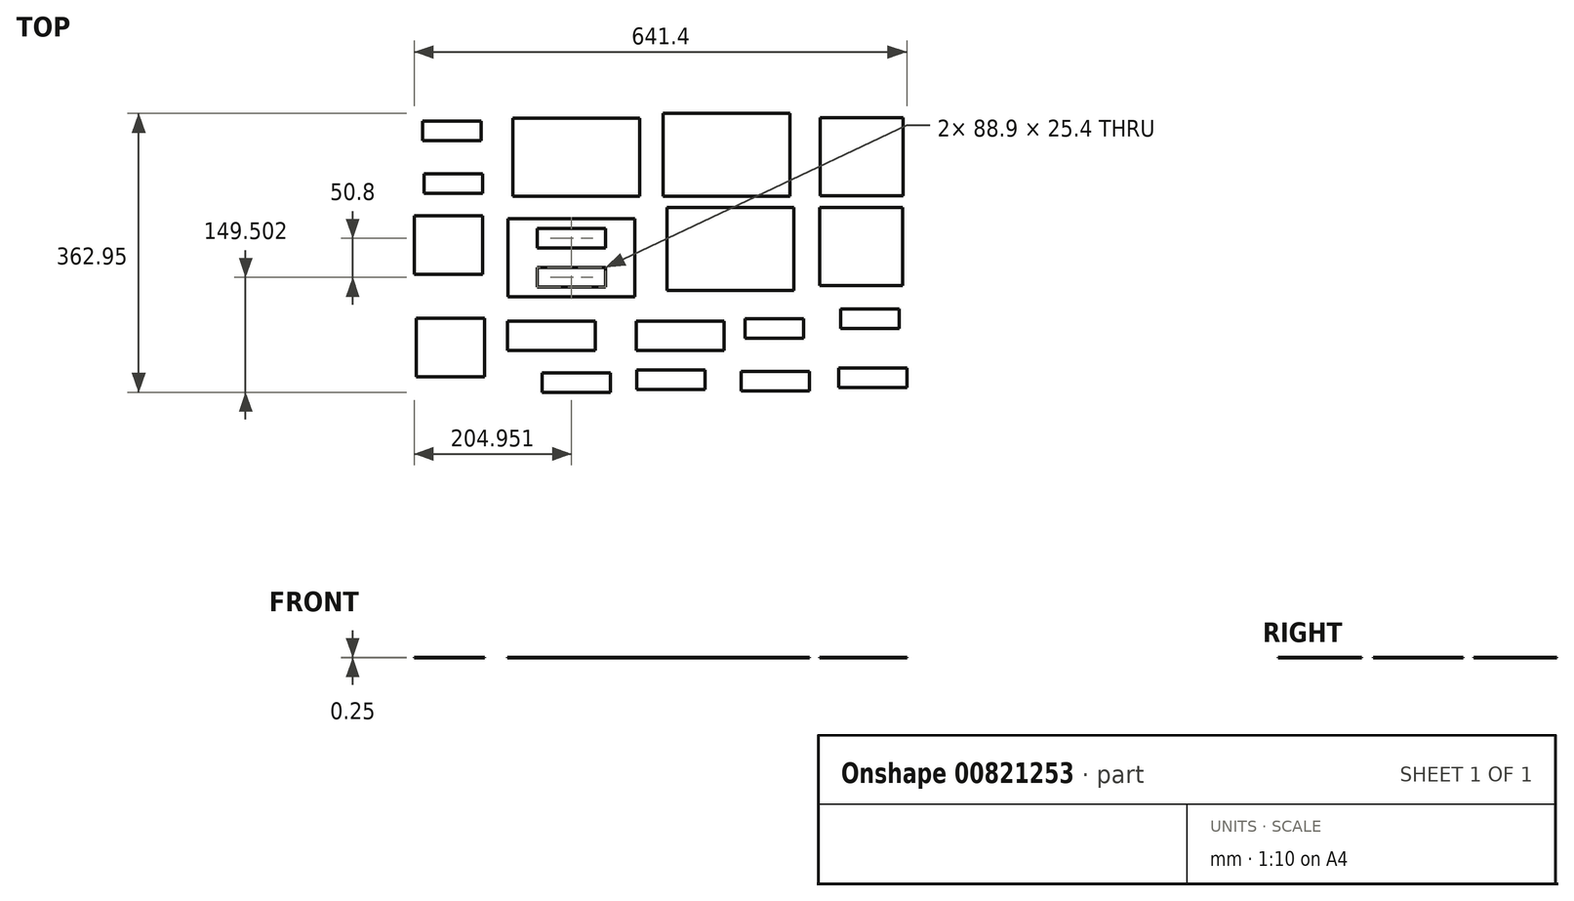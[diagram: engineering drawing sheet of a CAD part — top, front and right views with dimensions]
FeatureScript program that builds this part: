
annotation { "Feature Type Name" : "Feature", "Feature Type Description" : "" }
export const myFeature = defineFeature(function(context is Context, id is Id, definition is map)
    precondition{}
    {
        {
            assignVariable(context, id + "F0", {"name" : "th", "anyValue" : .25});
        }
        {
            var Q0;
            Q0=qCreatedBy(makeId("Top.planeOp"),FACE);
            var sketch = newSketch(context, id + "F1", { "sketchPlane" : qUnion([Q0])});
            skLineSegment(sketch, "E0.bottom", {"start": v(-461.23, 112.07) * mm, "end": v(-385.03, 112.07) * mm});
            skLineSegment(sketch, "E0.top", {"start": v(-461.23, 86.67) * mm, "end": v(-385.03, 86.67) * mm});
            skLineSegment(sketch, "E0.left", {"start": v(-461.23, 112.07) * mm, "end": v(-461.23, 86.67) * mm});
            skLineSegment(sketch, "E0.right", {"start": v(-385.03, 112.07) * mm, "end": v(-385.03, 86.67) * mm});
            skLineSegment(sketch, "E1.bottom", {"start": v(-459.53, 44.07) * mm, "end": v(-383.33, 44.07) * mm});
            skLineSegment(sketch, "E1.top", {"start": v(-459.53, 18.67) * mm, "end": v(-383.33, 18.67) * mm});
            skLineSegment(sketch, "E1.left", {"start": v(-459.53, 44.07) * mm, "end": v(-459.53, 18.67) * mm});
            skLineSegment(sketch, "E1.right", {"start": v(-383.33, 44.07) * mm, "end": v(-383.33, 18.67) * mm});
            skLineSegment(sketch, "E2.bottom", {"start": v(-472.28, -10.53) * mm, "end": v(-383.38, -10.53) * mm});
            skLineSegment(sketch, "E2.top", {"start": v(-472.28, -86.73) * mm, "end": v(-383.38, -86.73) * mm});
            skLineSegment(sketch, "E2.left", {"start": v(-472.28, -10.53) * mm, "end": v(-472.28, -86.73) * mm});
            skLineSegment(sketch, "E2.right", {"start": v(-383.38, -10.53) * mm, "end": v(-383.38, -86.73) * mm});
            skLineSegment(sketch, "E3.bottom", {"start": v(-469.73, -143.98) * mm, "end": v(-380.83, -143.98) * mm});
            skLineSegment(sketch, "E3.top", {"start": v(-469.73, -220.18) * mm, "end": v(-380.83, -220.18) * mm});
            skLineSegment(sketch, "E3.left", {"start": v(-469.73, -143.98) * mm, "end": v(-469.73, -220.18) * mm});
            skLineSegment(sketch, "E3.right", {"start": v(-380.83, -143.98) * mm, "end": v(-380.83, -220.18) * mm});
            skLineSegment(sketch, "E4.bottom", {"start": v(-343.93, 116.02) * mm, "end": v(-178.83, 116.02) * mm});
            skLineSegment(sketch, "E4.top", {"start": v(-343.93, 14.42) * mm, "end": v(-178.83, 14.42) * mm});
            skLineSegment(sketch, "E4.left", {"start": v(-343.93, 116.02) * mm, "end": v(-343.93, 14.42) * mm});
            skLineSegment(sketch, "E4.right", {"start": v(-178.83, 116.02) * mm, "end": v(-178.83, 14.42) * mm});
            skLineSegment(sketch, "E5.bottom", {"start": v(-349.88, -14.88) * mm, "end": v(-184.78, -14.88) * mm});
            skLineSegment(sketch, "E5.top", {"start": v(-349.88, -116.48) * mm, "end": v(-184.78, -116.48) * mm});
            skLineSegment(sketch, "E5.left", {"start": v(-349.88, -14.88) * mm, "end": v(-349.88, -116.48) * mm});
            skLineSegment(sketch, "E5.right", {"start": v(-184.78, -14.88) * mm, "end": v(-184.78, -116.48) * mm});
            skLineSegment(sketch, "E6.bottom", {"start": v(-311.78, -27.58) * mm, "end": v(-222.88, -27.58) * mm});
            skLineSegment(sketch, "E6.top", {"start": v(-311.78, -52.98) * mm, "end": v(-222.88, -52.98) * mm});
            skLineSegment(sketch, "E6.left", {"start": v(-311.78, -27.58) * mm, "end": v(-311.78, -52.98) * mm});
            skLineSegment(sketch, "E6.right", {"start": v(-222.88, -27.58) * mm, "end": v(-222.88, -52.98) * mm});
            skLineSegment(sketch, "E7.bottom", {"start": v(-311.78, -78.38) * mm, "end": v(-222.88, -78.38) * mm});
            skLineSegment(sketch, "E7.top", {"start": v(-311.78, -103.78) * mm, "end": v(-222.88, -103.78) * mm});
            skLineSegment(sketch, "E7.left", {"start": v(-311.78, -78.38) * mm, "end": v(-311.78, -103.78) * mm});
            skLineSegment(sketch, "E7.right", {"start": v(-222.88, -78.38) * mm, "end": v(-222.88, -103.78) * mm});
            skLineSegment(sketch, "E8.bottom", {"start": v(-350.73, -148.08) * mm, "end": v(-236.43, -148.08) * mm});
            skLineSegment(sketch, "E8.top", {"start": v(-350.73, -186.18) * mm, "end": v(-236.43, -186.18) * mm});
            skLineSegment(sketch, "E8.left", {"start": v(-350.73, -148.08) * mm, "end": v(-350.73, -186.18) * mm});
            skLineSegment(sketch, "E8.right", {"start": v(-236.43, -148.08) * mm, "end": v(-236.43, -186.18) * mm});
            skLineSegment(sketch, "E9.bottom", {"start": v(-305.68, -215.18) * mm, "end": v(-216.78, -215.18) * mm});
            skLineSegment(sketch, "E9.top", {"start": v(-305.68, -240.58) * mm, "end": v(-216.78, -240.58) * mm});
            skLineSegment(sketch, "E9.left", {"start": v(-305.68, -215.18) * mm, "end": v(-305.68, -240.58) * mm});
            skLineSegment(sketch, "E9.right", {"start": v(-216.78, -215.18) * mm, "end": v(-216.78, -240.58) * mm});
            skLineSegment(sketch, "E10.bottom", {"start": v(-183.28, -148.08) * mm, "end": v(-68.98, -148.08) * mm});
            skLineSegment(sketch, "E10.top", {"start": v(-183.28, -186.18) * mm, "end": v(-68.98, -186.18) * mm});
            skLineSegment(sketch, "E10.left", {"start": v(-183.28, -148.08) * mm, "end": v(-183.28, -186.18) * mm});
            skLineSegment(sketch, "E10.right", {"start": v(-68.98, -148.08) * mm, "end": v(-68.98, -186.18) * mm});
            skLineSegment(sketch, "E11.bottom", {"start": v(-182.43, -211.78) * mm, "end": v(-93.53, -211.78) * mm});
            skLineSegment(sketch, "E11.top", {"start": v(-182.43, -237.18) * mm, "end": v(-93.53, -237.18) * mm});
            skLineSegment(sketch, "E11.left", {"start": v(-182.43, -211.78) * mm, "end": v(-182.43, -237.18) * mm});
            skLineSegment(sketch, "E11.right", {"start": v(-93.53, -211.78) * mm, "end": v(-93.53, -237.18) * mm});
            skLineSegment(sketch, "E12.bottom", {"start": v(-41.33, -144.63) * mm, "end": v(34.87, -144.63) * mm});
            skLineSegment(sketch, "E12.top", {"start": v(-41.33, -170.03) * mm, "end": v(34.87, -170.03) * mm});
            skLineSegment(sketch, "E12.left", {"start": v(-41.33, -144.63) * mm, "end": v(-41.33, -170.03) * mm});
            skLineSegment(sketch, "E12.right", {"start": v(34.87, -144.63) * mm, "end": v(34.87, -170.03) * mm});
            skLineSegment(sketch, "E13.bottom", {"start": v(-46.43, -213.48) * mm, "end": v(42.47, -213.48) * mm});
            skLineSegment(sketch, "E13.top", {"start": v(-46.43, -238.88) * mm, "end": v(42.47, -238.88) * mm});
            skLineSegment(sketch, "E13.left", {"start": v(-46.43, -213.48) * mm, "end": v(-46.43, -238.88) * mm});
            skLineSegment(sketch, "E13.right", {"start": v(42.47, -213.48) * mm, "end": v(42.47, -238.88) * mm});
            skLineSegment(sketch, "E14.bottom", {"start": v(80.22, -234.63) * mm, "end": v(169.12, -234.63) * mm});
            skLineSegment(sketch, "E14.top", {"start": v(80.22, -209.23) * mm, "end": v(169.12, -209.23) * mm});
            skLineSegment(sketch, "E14.left", {"start": v(80.22, -234.63) * mm, "end": v(80.22, -209.23) * mm});
            skLineSegment(sketch, "E14.right", {"start": v(169.12, -234.63) * mm, "end": v(169.12, -209.23) * mm});
            skLineSegment(sketch, "E15.bottom", {"start": v(82.77, -157.28) * mm, "end": v(158.97, -157.28) * mm});
            skLineSegment(sketch, "E15.top", {"start": v(82.77, -131.88) * mm, "end": v(158.97, -131.88) * mm});
            skLineSegment(sketch, "E15.left", {"start": v(82.77, -157.28) * mm, "end": v(82.77, -131.88) * mm});
            skLineSegment(sketch, "E15.right", {"start": v(158.97, -157.28) * mm, "end": v(158.97, -131.88) * mm});
            skLineSegment(sketch, "E16.bottom", {"start": v(55.57, -101.6) * mm, "end": v(163.52, -101.6) * mm});
            skLineSegment(sketch, "E16.top", {"start": v(55.57, 0) * mm, "end": v(163.52, 0) * mm});
            skLineSegment(sketch, "E16.left", {"start": v(55.57, -101.6) * mm, "end": v(55.57, 0) * mm});
            skLineSegment(sketch, "E16.right", {"start": v(163.52, -101.6) * mm, "end": v(163.52, 0) * mm});
            skLineSegment(sketch, "E17.bottom", {"start": v(56.42, 15.27) * mm, "end": v(164.37, 15.27) * mm});
            skLineSegment(sketch, "E17.top", {"start": v(56.42, 116.87) * mm, "end": v(164.37, 116.87) * mm});
            skLineSegment(sketch, "E17.left", {"start": v(56.42, 15.27) * mm, "end": v(56.42, 116.87) * mm});
            skLineSegment(sketch, "E17.right", {"start": v(164.37, 15.27) * mm, "end": v(164.37, 116.87) * mm});
            skLineSegment(sketch, "E18.bottom", {"start": v(-148.43, 122.37) * mm, "end": v(16.67, 122.37) * mm});
            skLineSegment(sketch, "E18.top", {"start": v(-148.43, 14.42) * mm, "end": v(16.67, 14.42) * mm});
            skLineSegment(sketch, "E18.left", {"start": v(-148.43, 122.37) * mm, "end": v(-148.43, 14.42) * mm});
            skLineSegment(sketch, "E18.right", {"start": v(16.67, 122.37) * mm, "end": v(16.67, 14.42) * mm});
            skLineSegment(sketch, "E19.bottom", {"start": v(-143.33, 0) * mm, "end": v(21.77, 0) * mm});
            skLineSegment(sketch, "E19.top", {"start": v(-143.33, -107.95) * mm, "end": v(21.77, -107.95) * mm});
            skLineSegment(sketch, "E19.left", {"start": v(-143.33, 0) * mm, "end": v(-143.33, -107.95) * mm});
            skLineSegment(sketch, "E19.right", {"start": v(21.77, 0) * mm, "end": v(21.77, -107.95) * mm});
            skLineSegment(sketch, "E20", {"start": v(-349.88, -65.68) * mm, "end": v(-184.78, -65.68) * mm, "construction": true});
            skSolve(sketch);
        }
        {
            var Q0;
            Q0 = qSketchRegion(id + "F1", true);
            extrude(context, id + "F2", {"entities" : qUnion([Q0]), "depth" : (getVariable(context, 'th')) * mm, "offsetDistance" : 25.4 * mm});
        }
    });
